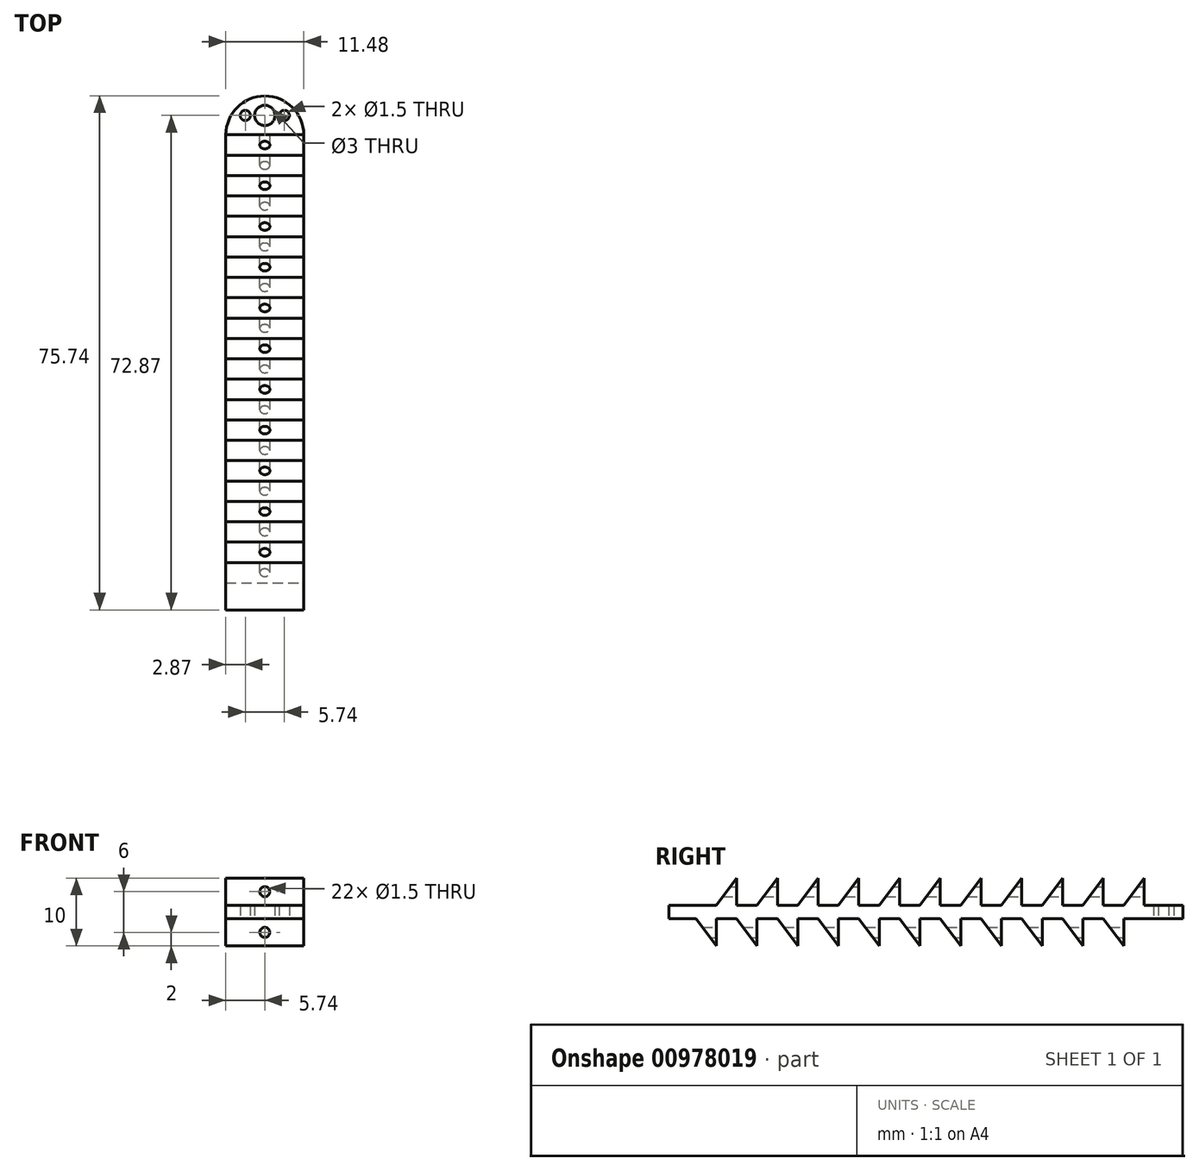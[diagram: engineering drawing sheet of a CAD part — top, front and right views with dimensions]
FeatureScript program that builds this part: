
annotation { "Feature Type Name" : "Feature", "Feature Type Description" : "" }
export const myFeature = defineFeature(function(context is Context, id is Id, definition is map)
    precondition{}
    {
        {
            var Q0;
            Q0=qCreatedBy(makeId("Top.planeOp"),FACE);
            var sketch = newSketch(context, id + "F0", { "sketchPlane" : qUnion([Q0])});
            skLineSegment(sketch, "E0.top", {"start": v(5.74, -35) * mm, "end": v(-5.74, -35) * mm});
            skLineSegment(sketch, "E0.left", {"start": v(5.74, 35) * mm, "end": v(5.74, -35) * mm});
            skLineSegment(sketch, "E0.right", {"start": v(-5.74, 35) * mm, "end": v(-5.74, -35) * mm});
            skPoint(sketch, "E0.middle", {"position": v(0, 0) * mm});
            skArc(sketch, "E1", {"start": v(5.74, 35) * mm, "mid": v(0, 40.74) * mm, "end": v(-5.74, 35) * mm});
            skLineSegment(sketch, "E2", {"start": v(-5.74, 35) * mm, "end": v(0, 40.74) * mm, "construction": true});
            skLineSegment(sketch, "E3", {"start": v(0, 40.74) * mm, "end": v(5.74, 35) * mm, "construction": true});
            skCircle(sketch, "E4", {"center": v(-2.87, 37.87) * mm, "radius": 0.75 * mm});
            skCircle(sketch, "E5", {"center": v(2.87, 37.87) * mm, "radius": 0.75 * mm});
            skCircle(sketch, "E6", {"center": v(0, 37.87) * mm, "radius": 1.5 * mm});
            skSolve(sketch);
        }
        {
            var Q0;
            Q0 = qSketchRegion(id + "F0", true);
            extrude(context, id + "F1", {"entities" : qUnion([Q0]), "endBound" : BoundingType.SYMMETRIC, "depth" : 2 * mm, "offsetDistance" : 25 * mm});
        }
        {
            var Q0;
            Q0=makeQuery(id+"F1.opExtrude","SWEPT_FACE",FACE,{"disambiguationData":[OSD([sQuery(id+"F0.wireOp",EDGE,"E0.left")])]});
            var sketch = newSketch(context, id + "F2", { "sketchPlane" : qUnion([Q0])});
            skLineSegment(sketch, "E7", {"start": v(35, 1) * mm, "end": v(35, 5) * mm});
            skLineSegment(sketch, "E8", {"start": v(35, 5) * mm, "end": v(32, 1) * mm});
            skLineSegment(sketch, "E9", {"start": v(32, 1) * mm, "end": v(35, 1) * mm});
            skLineSegment(sketch, "E10", {"start": v(32, -1) * mm, "end": v(32, -5) * mm});
            skLineSegment(sketch, "E11", {"start": v(32, -5) * mm, "end": v(29, -1) * mm});
            skLineSegment(sketch, "E12", {"start": v(29, -1) * mm, "end": v(32, -1) * mm});
            skLineSegment(sketch, "E13.1.0.0", {"start": v(29, 1) * mm, "end": v(29, 5) * mm});
            skLineSegment(sketch, "E13.1.0.1", {"start": v(29, 5) * mm, "end": v(26, 1) * mm});
            skLineSegment(sketch, "E13.1.0.2", {"start": v(26, 1) * mm, "end": v(29, 1) * mm});
            skLineSegment(sketch, "E13.1.0.3", {"start": v(26, -1) * mm, "end": v(26, -5) * mm});
            skLineSegment(sketch, "E13.1.0.4", {"start": v(26, -5) * mm, "end": v(23, -1) * mm});
            skLineSegment(sketch, "E13.1.0.5", {"start": v(23, -1) * mm, "end": v(26, -1) * mm});
            skLineSegment(sketch, "E13.2.0.0", {"start": v(23, 1) * mm, "end": v(23, 5) * mm});
            skLineSegment(sketch, "E13.2.0.1", {"start": v(23, 5) * mm, "end": v(20, 1) * mm});
            skLineSegment(sketch, "E13.2.0.2", {"start": v(20, 1) * mm, "end": v(23, 1) * mm});
            skLineSegment(sketch, "E13.2.0.3", {"start": v(20, -1) * mm, "end": v(20, -5) * mm});
            skLineSegment(sketch, "E13.2.0.4", {"start": v(20, -5) * mm, "end": v(17, -1) * mm});
            skLineSegment(sketch, "E13.2.0.5", {"start": v(17, -1) * mm, "end": v(20, -1) * mm});
            skLineSegment(sketch, "E13.3.0.0", {"start": v(17, 1) * mm, "end": v(17, 5) * mm});
            skLineSegment(sketch, "E13.3.0.1", {"start": v(17, 5) * mm, "end": v(14, 1) * mm});
            skLineSegment(sketch, "E13.3.0.2", {"start": v(14, 1) * mm, "end": v(17, 1) * mm});
            skLineSegment(sketch, "E13.3.0.3", {"start": v(14, -1) * mm, "end": v(14, -5) * mm});
            skLineSegment(sketch, "E13.3.0.4", {"start": v(14, -5) * mm, "end": v(11, -1) * mm});
            skLineSegment(sketch, "E13.3.0.5", {"start": v(11, -1) * mm, "end": v(14, -1) * mm});
            skLineSegment(sketch, "E13.4.0.0", {"start": v(11, 1) * mm, "end": v(11, 5) * mm});
            skLineSegment(sketch, "E13.4.0.1", {"start": v(11, 5) * mm, "end": v(8, 1) * mm});
            skLineSegment(sketch, "E13.4.0.2", {"start": v(8, 1) * mm, "end": v(11, 1) * mm});
            skLineSegment(sketch, "E13.4.0.3", {"start": v(8, -1) * mm, "end": v(8, -5) * mm});
            skLineSegment(sketch, "E13.4.0.4", {"start": v(8, -5) * mm, "end": v(5, -1) * mm});
            skLineSegment(sketch, "E13.4.0.5", {"start": v(5, -1) * mm, "end": v(8, -1) * mm});
            skLineSegment(sketch, "E13.5.0.0", {"start": v(5, 1) * mm, "end": v(5, 5) * mm});
            skLineSegment(sketch, "E13.5.0.1", {"start": v(5, 5) * mm, "end": v(2, 1) * mm});
            skLineSegment(sketch, "E13.5.0.2", {"start": v(2, 1) * mm, "end": v(5, 1) * mm});
            skLineSegment(sketch, "E13.5.0.3", {"start": v(2, -1) * mm, "end": v(2, -5) * mm});
            skLineSegment(sketch, "E13.5.0.4", {"start": v(2, -5) * mm, "end": v(-1, -1) * mm});
            skLineSegment(sketch, "E13.5.0.5", {"start": v(-1, -1) * mm, "end": v(2, -1) * mm});
            skLineSegment(sketch, "E13.6.0.0", {"start": v(-1, 1) * mm, "end": v(-1, 5) * mm});
            skLineSegment(sketch, "E13.6.0.1", {"start": v(-1, 5) * mm, "end": v(-4, 1) * mm});
            skLineSegment(sketch, "E13.6.0.2", {"start": v(-4, 1) * mm, "end": v(-1, 1) * mm});
            skLineSegment(sketch, "E13.6.0.3", {"start": v(-4, -1) * mm, "end": v(-4, -5) * mm});
            skLineSegment(sketch, "E13.6.0.4", {"start": v(-4, -5) * mm, "end": v(-7, -1) * mm});
            skLineSegment(sketch, "E13.6.0.5", {"start": v(-7, -1) * mm, "end": v(-4, -1) * mm});
            skLineSegment(sketch, "E13.7.0.0", {"start": v(-7, 1) * mm, "end": v(-7, 5) * mm});
            skLineSegment(sketch, "E13.7.0.1", {"start": v(-7, 5) * mm, "end": v(-10, 1) * mm});
            skLineSegment(sketch, "E13.7.0.2", {"start": v(-10, 1) * mm, "end": v(-7, 1) * mm});
            skLineSegment(sketch, "E13.7.0.3", {"start": v(-10, -1) * mm, "end": v(-10, -5) * mm});
            skLineSegment(sketch, "E13.7.0.4", {"start": v(-10, -5) * mm, "end": v(-13, -1) * mm});
            skLineSegment(sketch, "E13.7.0.5", {"start": v(-13, -1) * mm, "end": v(-10, -1) * mm});
            skLineSegment(sketch, "E13.8.0.0", {"start": v(-13, 1) * mm, "end": v(-13, 5) * mm});
            skLineSegment(sketch, "E13.8.0.1", {"start": v(-13, 5) * mm, "end": v(-16, 1) * mm});
            skLineSegment(sketch, "E13.8.0.2", {"start": v(-16, 1) * mm, "end": v(-13, 1) * mm});
            skLineSegment(sketch, "E13.8.0.3", {"start": v(-16, -1) * mm, "end": v(-16, -5) * mm});
            skLineSegment(sketch, "E13.8.0.4", {"start": v(-16, -5) * mm, "end": v(-19, -1) * mm});
            skLineSegment(sketch, "E13.8.0.5", {"start": v(-19, -1) * mm, "end": v(-16, -1) * mm});
            skLineSegment(sketch, "E13.9.0.0", {"start": v(-19, 1) * mm, "end": v(-19, 5) * mm});
            skLineSegment(sketch, "E13.9.0.1", {"start": v(-19, 5) * mm, "end": v(-22, 1) * mm});
            skLineSegment(sketch, "E13.9.0.2", {"start": v(-22, 1) * mm, "end": v(-19, 1) * mm});
            skLineSegment(sketch, "E13.9.0.3", {"start": v(-22, -1) * mm, "end": v(-22, -5) * mm});
            skLineSegment(sketch, "E13.9.0.4", {"start": v(-22, -5) * mm, "end": v(-25, -1) * mm});
            skLineSegment(sketch, "E13.9.0.5", {"start": v(-25, -1) * mm, "end": v(-22, -1) * mm});
            skLineSegment(sketch, "E13.10.0.0", {"start": v(-25, 1) * mm, "end": v(-25, 5) * mm});
            skLineSegment(sketch, "E13.10.0.1", {"start": v(-25, 5) * mm, "end": v(-28, 1) * mm});
            skLineSegment(sketch, "E13.10.0.2", {"start": v(-28, 1) * mm, "end": v(-25, 1) * mm});
            skLineSegment(sketch, "E13.10.0.3", {"start": v(-28, -1) * mm, "end": v(-28, -5) * mm});
            skLineSegment(sketch, "E13.10.0.4", {"start": v(-28, -5) * mm, "end": v(-31, -1) * mm});
            skLineSegment(sketch, "E13.10.0.5", {"start": v(-31, -1) * mm, "end": v(-28, -1) * mm});
            skLineSegment(sketch, "E13.direction1", {"start": v(35, 1) * mm, "end": v(29, 1) * mm, "construction": true});
            skSolve(sketch);
        }
        {
            var Q0;
            Q0 = qSketchRegion(id + "F2", true);
            extrude(context, id + "F3", {"entities" : qUnion([Q0]), "operationType" : NewBodyOperationType.ADD, "oppositeDirection" : true, "depth" : 11.48 * mm, "offsetDistance" : 25 * mm});
        }
        {
            var Q0;
            Q0=makeQuery(id+"F3.opExtrude","SWEPT_FACE",FACE,{"disambiguationData":[OSD([sQuery(id+"F2.wireOp",EDGE,"E7")])]});
            var sketch = newSketch(context, id + "F4", { "sketchPlane" : qUnion([Q0])});
            skLineSegment(sketch, "E14", {"start": v(-5.74, 5) * mm, "end": v(5.74, 1) * mm, "construction": true});
            skLineSegment(sketch, "E15", {"start": v(-5.74, 1) * mm, "end": v(5.74, 5) * mm, "construction": true});
            skCircle(sketch, "E16", {"center": v(0, 3) * mm, "radius": 0.75 * mm});
            skSolve(sketch);
        }
        {
            var Q0;
            Q0 = qSketchRegion(id + "F4", true);
            extrude(context, id + "F5", {"entities" : qUnion([Q0]), "operationType" : NewBodyOperationType.REMOVE, "oppositeDirection" : true, "depth" : 70 * mm, "offsetDistance" : 25 * mm});
        }
        {
            var Q0;
            Q0=makeQuery(id+"F3.opExtrude","SWEPT_FACE",FACE,{"disambiguationData":[OSD([sQuery(id+"F2.wireOp",EDGE,"E10")])]});
            var sketch = newSketch(context, id + "F6", { "sketchPlane" : qUnion([Q0])});
            skLineSegment(sketch, "E17", {"start": v(-5.74, -5) * mm, "end": v(5.74, -1) * mm, "construction": true});
            skLineSegment(sketch, "E18", {"start": v(5.74, -5) * mm, "end": v(-5.74, -1) * mm, "construction": true});
            skCircle(sketch, "E19", {"center": v(0, -3) * mm, "radius": 0.75 * mm});
            skSolve(sketch);
        }
        {
            var Q0;
            Q0 = qSketchRegion(id + "F6", true);
            extrude(context, id + "F7", {"entities" : qUnion([Q0]), "operationType" : NewBodyOperationType.REMOVE, "oppositeDirection" : true, "depth" : 70 * mm, "offsetDistance" : 25 * mm});
        }
    });
